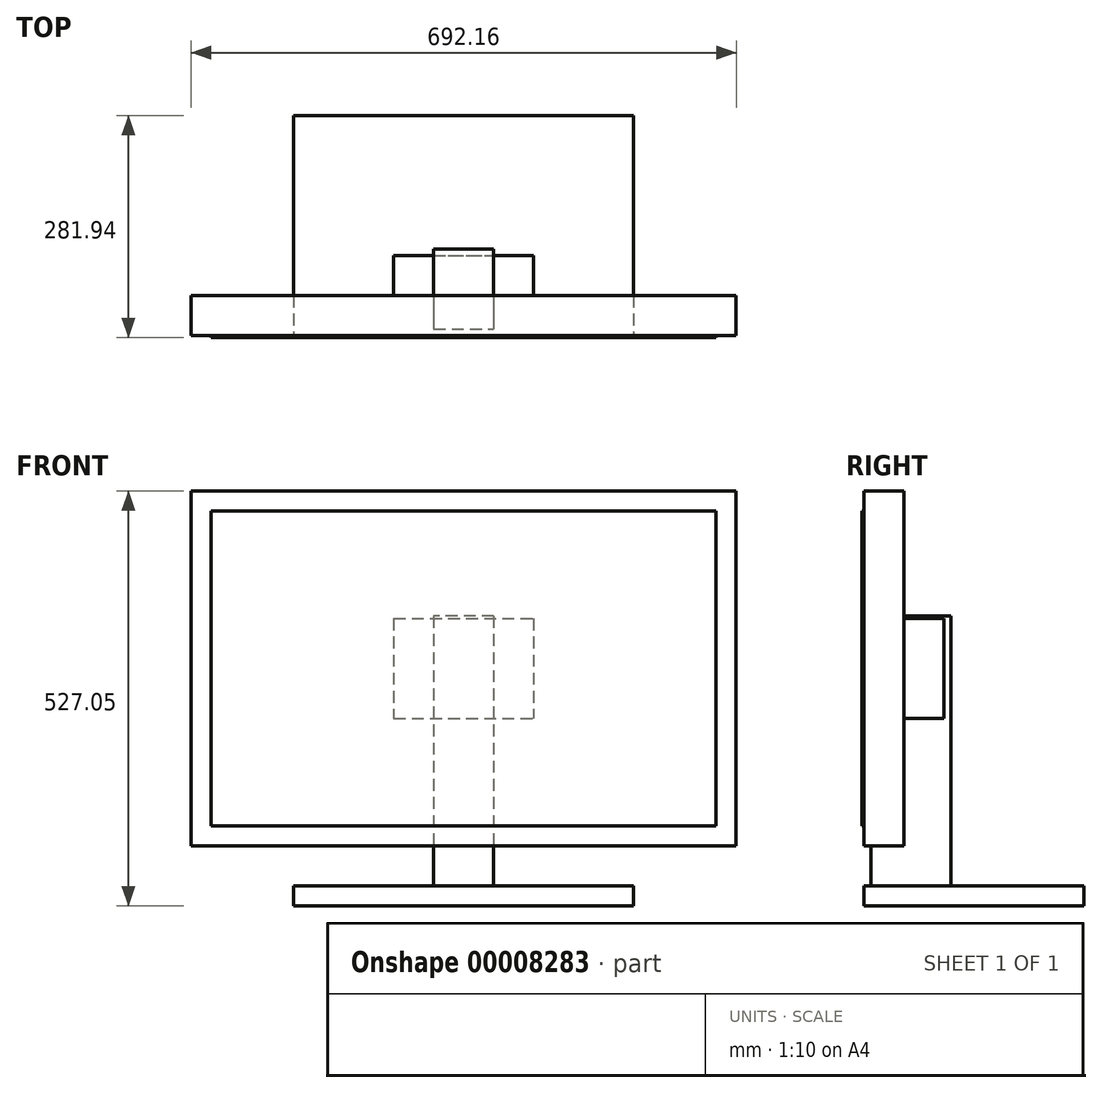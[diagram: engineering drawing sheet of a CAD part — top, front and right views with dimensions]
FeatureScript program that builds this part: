
annotation { "Feature Type Name" : "Feature", "Feature Type Description" : "" }
export const myFeature = defineFeature(function(context is Context, id is Id, definition is map)
    precondition{}
    {
        {
            var Q0;
            Q0=qCreatedBy(makeId("Front.planeOp"),FACE);
            var sketch = newSketch(context, id + "F0", { "sketchPlane" : qUnion([Q0])});
            skLineSegment(sketch, "E0.bottom", {"start": v(-346.07, 527.05) * mm, "end": v(346.07, 527.05) * mm});
            skLineSegment(sketch, "E0.top", {"start": v(-346.07, 76.2) * mm, "end": v(346.07, 76.2) * mm});
            skLineSegment(sketch, "E0.left", {"start": v(-346.08, 527.05) * mm, "end": v(-346.07, 76.2) * mm});
            skLineSegment(sketch, "E0.right", {"start": v(346.08, 527.05) * mm, "end": v(346.08, 76.2) * mm});
            skPoint(sketch, "E1", {"position": v(0, 76.2) * mm});
            skPoint(sketch, "E2", {"position": v(0, 527.05) * mm});
            skSolve(sketch);
        }
        {
            var Q0;
            Q0=makeQuery(id+"F0.imprint","IMPRINT",FACE,{"disambiguationData":[TD([[makeQuery(id+"F0.imprint","IMPRINT",EDGE,{"derivedFrom":sQuery(id+"F0.wireOp",EDGE,"E0.bottom")}),-1.0]])]});
            extrude(context, id + "F1", {"entities" : qUnion([Q0]), "depth" : 50.8 * mm});
        }
        {
            var Q0;
            Q0=qCreatedBy(makeId("Top.planeOp"),FACE);
            var sketch = newSketch(context, id + "F2", { "sketchPlane" : qUnion([Q0])});
            skLineSegment(sketch, "E3.bottom", {"start": v(-215.9, 228.6) * mm, "end": v(215.9, 228.6) * mm});
            skLineSegment(sketch, "E3.top", {"start": v(-215.9, -50.8) * mm, "end": v(215.9, -50.8) * mm});
            skLineSegment(sketch, "E3.left", {"start": v(-215.9, 228.6) * mm, "end": v(-215.9, -50.8) * mm});
            skLineSegment(sketch, "E3.right", {"start": v(215.9, 228.6) * mm, "end": v(215.9, -50.8) * mm});
            skPoint(sketch, "E4", {"position": v(0, -50.8) * mm});
            skSolve(sketch);
        }
        {
            var Q0;
            Q0=makeQuery(id+"F2.imprint","IMPRINT",FACE,{"disambiguationData":[TD([[makeQuery(id+"F2.imprint","IMPRINT",EDGE,{"derivedFrom":sQuery(id+"F2.wireOp",EDGE,"E3.bottom")}),-1.0]])]});
            extrude(context, id + "F3", {"entities" : qUnion([Q0]), "depth" : 25.4 * mm});
        }
        {
            var Q0;
            Q0=qCreatedBy(makeId("Top.planeOp"),FACE);
            var sketch = newSketch(context, id + "F4", { "sketchPlane" : qUnion([Q0])});
            skLineSegment(sketch, "E5.bottom", {"start": v(38.1, -42.37) * mm, "end": v(-38.1, -42.37) * mm});
            skLineSegment(sketch, "E5.top", {"start": v(38.1, 59.23) * mm, "end": v(-38.1, 59.23) * mm});
            skLineSegment(sketch, "E5.left", {"start": v(38.1, -42.37) * mm, "end": v(38.1, 59.23) * mm});
            skLineSegment(sketch, "E5.right", {"start": v(-38.1, -42.37) * mm, "end": v(-38.1, 59.23) * mm});
            skPoint(sketch, "E6", {"position": v(0, -42.37) * mm});
            skSolve(sketch);
        }
        {
            var Q0;
            Q0 = qSketchRegion(id + "F4", true);
            extrude(context, id + "F5", {"entities" : qUnion([Q0]), "operationType" : NewBodyOperationType.ADD, "depth" : 368.3 * mm});
        }
        {
            var Q0;
            Q0=qCreatedBy(makeId("Front.planeOp"),FACE);
            var sketch = newSketch(context, id + "F6", { "sketchPlane" : qUnion([Q0])});
            skPoint(sketch, "E7", {"position": v(0, 238.12) * mm});
            skLineSegment(sketch, "E8.bottom", {"start": v(-88.9, 365.12) * mm, "end": v(88.9, 365.12) * mm});
            skLineSegment(sketch, "E8.top", {"start": v(-88.9, 238.12) * mm, "end": v(88.9, 238.12) * mm});
            skLineSegment(sketch, "E8.left", {"start": v(-88.9, 365.12) * mm, "end": v(-88.9, 238.12) * mm});
            skLineSegment(sketch, "E8.right", {"start": v(88.9, 365.12) * mm, "end": v(88.9, 238.12) * mm});
            skPoint(sketch, "E9", {"position": v(-346.07, 301.62) * mm});
            skPoint(sketch, "E10", {"position": v(-88.9, 301.62) * mm});
            skSolve(sketch);
        }
        {
            var Q0;
            Q0 = qSketchRegion(id + "F6", true);
            extrude(context, id + "F7", {"entities" : qUnion([Q0]), "oppositeDirection" : true, "depth" : 50.8 * mm});
        }
        {
            var Q0;
            Q0=makeQuery(id+"F1.opExtrude","CAP_FACE",FACE,{"disambiguationData":[OSD([sQuery(id+"F0.wireOp",EDGE,"E0.bottom"),sQuery(id+"F0.wireOp",EDGE,"E0.top"),sQuery(id+"F0.wireOp",EDGE,"E0.left"),sQuery(id+"F0.wireOp",EDGE,"E0.right")])],"isStart":false});
            var sketch = newSketch(context, id + "F8", { "sketchPlane" : qUnion([Q0])});
            skLineSegment(sketch, "E11.bottom", {"start": v(-320.68, 501.65) * mm, "end": v(320.68, 501.65) * mm});
            skLineSegment(sketch, "E11.top", {"start": v(-320.68, 101.6) * mm, "end": v(320.68, 101.6) * mm});
            skLineSegment(sketch, "E11.left", {"start": v(-320.68, 501.65) * mm, "end": v(-320.68, 101.6) * mm});
            skLineSegment(sketch, "E11.right", {"start": v(320.67, 501.65) * mm, "end": v(320.67, 101.6) * mm});
            skPoint(sketch, "E12", {"position": v(0, 76.2) * mm});
            skPoint(sketch, "E13", {"position": v(-346.07, 301.62) * mm});
            skPoint(sketch, "E14", {"position": v(-320.67, 301.62) * mm});
            skPoint(sketch, "E15", {"position": v(0, 101.6) * mm});
            skSolve(sketch);
        }
        {
            var Q0;
            Q0 = qSketchRegion(id + "F8", true);
            extrude(context, id + "F9", {"entities" : qUnion([Q0]), "depth" : 2.54 * mm});
        }
    });
